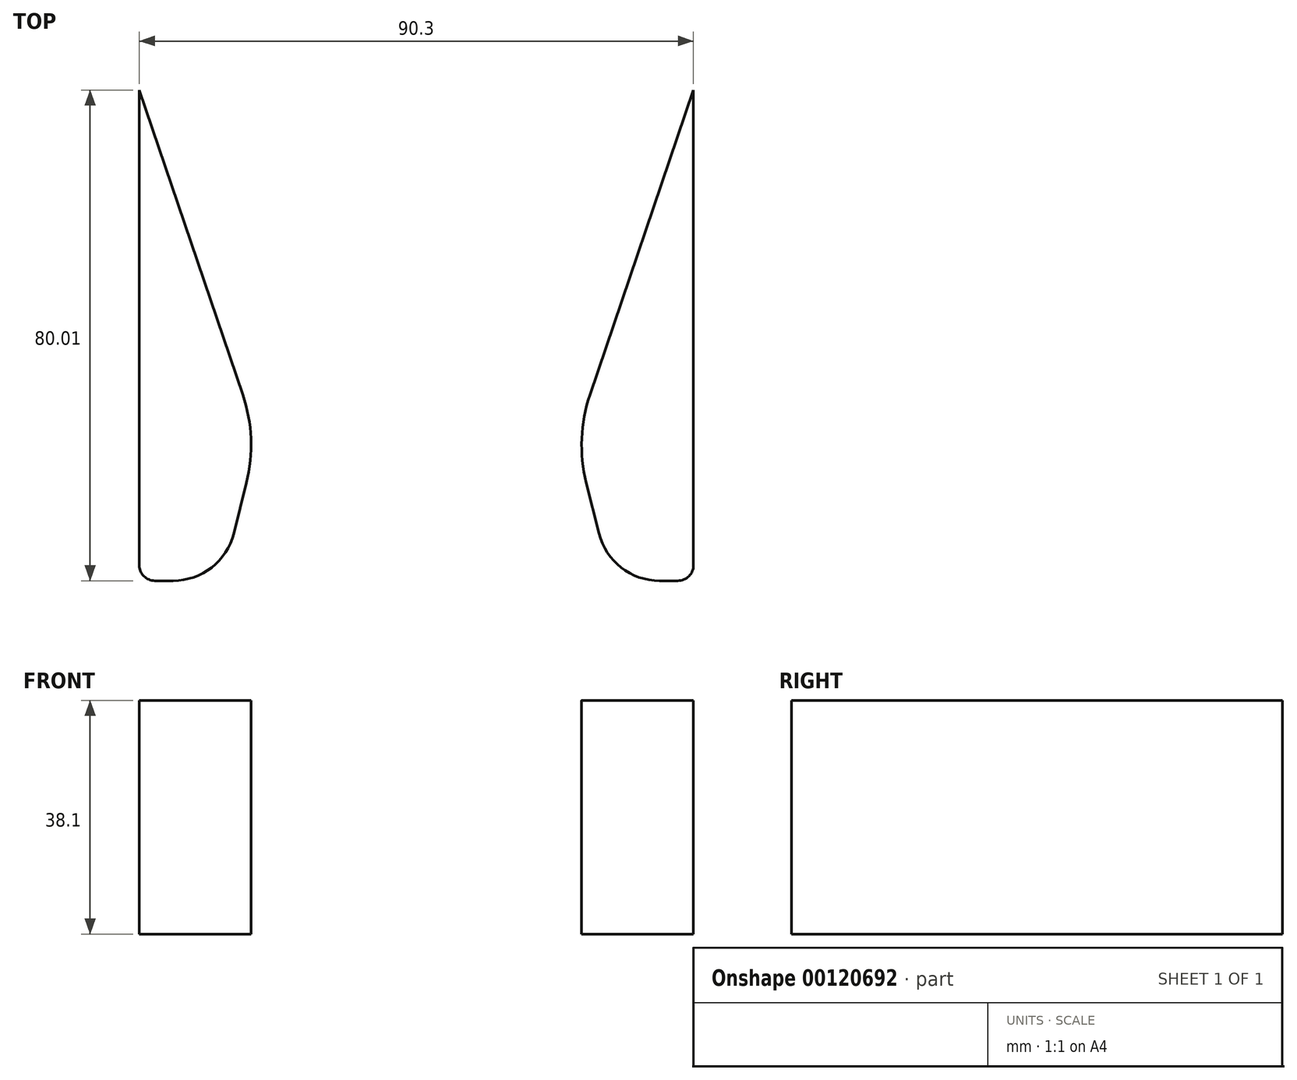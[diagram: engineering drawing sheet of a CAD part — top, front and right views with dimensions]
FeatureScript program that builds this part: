
annotation { "Feature Type Name" : "Feature", "Feature Type Description" : "" }
export const myFeature = defineFeature(function(context is Context, id is Id, definition is map)
    precondition{}
    {
        {
            var Q0;
            Q0=qCreatedBy(makeId("Top.planeOp"),FACE);
            var sketch = newSketch(context, id + "F0", { "sketchPlane" : qUnion([Q0])});
            skLineSegment(sketch, "E0", {"start": v(-45.15, -28.78) * mm, "end": v(-45.15, 51.23) * mm});
            skLineSegment(sketch, "E1", {"start": v(-45.15, 51.23) * mm, "end": v(-25.88, -5.55) * mm});
            skLineSegment(sketch, "E2", {"start": v(-25.88, -5.55) * mm, "end": v(-31.69, -28.78) * mm});
            skLineSegment(sketch, "E3", {"start": v(-31.69, -28.78) * mm, "end": v(-45.15, -28.78) * mm});
            skLineSegment(sketch, "E4.MirrorCS", {"start": v(45.15, 51.23) * mm, "end": v(25.88, -5.55) * mm});
            skLineSegment(sketch, "E5.MirrorCS", {"start": v(25.88, -5.55) * mm, "end": v(31.69, -28.78) * mm});
            skLineSegment(sketch, "E6.MirrorCS", {"start": v(31.69, -28.78) * mm, "end": v(45.15, -28.78) * mm});
            skLineSegment(sketch, "E7.MirrorCS", {"start": v(45.15, -28.78) * mm, "end": v(45.15, 51.23) * mm});
            skSolve(sketch);
        }
        {
            var Q0;
            Q0=makeQuery(id+"F0.imprint","IMPRINT",FACE,{"disambiguationData":[TD([[makeQuery(id+"F0.imprint","IMPRINT",EDGE,{"derivedFrom":sQuery(id+"F0.wireOp",EDGE,"E0")}),-1.0]])]});
            var Q1;
            Q1=makeQuery(id+"F0.imprint","IMPRINT",FACE,{"disambiguationData":[TD([[makeQuery(id+"F0.imprint","IMPRINT",EDGE,{"derivedFrom":sQuery(id+"F0.wireOp",EDGE,"E4.MirrorCS")}),1.0]])]});
            extrude(context, id + "F1", {"entities" : qUnion([Q0, Q1]), "oppositeDirection" : true, "depth" : 38.1 * mm});
        }
        {
            var Q0;
            Q0=makeQuery(id+"F1.opExtrude","SWEPT_EDGE",EDGE,{"disambiguationData":[OSD([sQuery(id+"F0.wireOp",EDGE,"E4.MirrorCS"),sQuery(id+"F0.wireOp",EDGE,"E5.MirrorCS")])]});
            fillet(context, id + "F2", {"entities" : qUnion([Q0]), "radius" : 25.4 * mm, "tangentPropagation" : true, "allowEdgeOverflow" : false});
        }
        {
            var Q0;
            Q0=makeQuery(id+"F1.opExtrude","SWEPT_EDGE",EDGE,{"disambiguationData":[OSD([sQuery(id+"F0.wireOp",EDGE,"E5.MirrorCS"),sQuery(id+"F0.wireOp",EDGE,"E6.MirrorCS")])]});
            fillet(context, id + "F3", {"entities" : qUnion([Q0]), "radius" : 10.16 * mm, "tangentPropagation" : true, "allowEdgeOverflow" : false});
        }
        {
            var Q0;
            Q0=makeQuery(id+"F1.opExtrude","SWEPT_EDGE",EDGE,{"disambiguationData":[OSD([sQuery(id+"F0.wireOp",EDGE,"E6.MirrorCS"),sQuery(id+"F0.wireOp",EDGE,"E7.MirrorCS")])]});
            fillet(context, id + "F4", {"entities" : qUnion([Q0]), "radius" : 2.54 * mm, "tangentPropagation" : true, "allowEdgeOverflow" : false});
        }
        {
            var Q0;
            Q0=makeQuery(id+"F1.opExtrude","SWEPT_EDGE",EDGE,{"disambiguationData":[OSD([sQuery(id+"F0.wireOp",EDGE,"E1"),sQuery(id+"F0.wireOp",EDGE,"E2")])]});
            fillet(context, id + "F5", {"entities" : qUnion([Q0]), "radius" : 25.4 * mm, "tangentPropagation" : true, "allowEdgeOverflow" : false});
        }
        {
            var Q0;
            Q0=makeQuery(id+"F1.opExtrude","SWEPT_EDGE",EDGE,{"disambiguationData":[OSD([sQuery(id+"F0.wireOp",EDGE,"E2"),sQuery(id+"F0.wireOp",EDGE,"E3")])]});
            fillet(context, id + "F6", {"entities" : qUnion([Q0]), "radius" : 10.16 * mm, "tangentPropagation" : true, "allowEdgeOverflow" : false});
        }
        {
            var Q0;
            Q0=makeQuery(id+"F1.opExtrude","SWEPT_EDGE",EDGE,{"disambiguationData":[OSD([sQuery(id+"F0.wireOp",EDGE,"E0"),sQuery(id+"F0.wireOp",EDGE,"E3")])]});
            fillet(context, id + "F7", {"entities" : qUnion([Q0]), "radius" : 2.54 * mm, "tangentPropagation" : true, "allowEdgeOverflow" : false});
        }
    });
